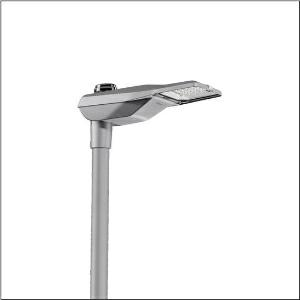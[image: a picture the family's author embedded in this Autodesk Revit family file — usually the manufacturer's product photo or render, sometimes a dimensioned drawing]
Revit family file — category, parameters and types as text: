
# Revit family: streetlight_sl_21_micro___st0_8a_5xe5c37n08db_0c9a
name_source: partatom
category: Lighting Fixtures
units: mm (PartAtom-declared; Revit-internal decimal feet)

## family parameters
Cut with Voids When Loaded = No
Host = Face
Light Source = No
Part Type = Normal
Room Calculation Point = No
Round Connector Dimension = Use Diameter
Shared = No

## types (1)
- --- (1 x LED, 5110 lm, 39.1 W, 3000K)
    Apparent Load = 39 VA
    CIE Flux Codes = 38 75 97 100 100
    Color Rendering = 70
    Color Temperature = 3000K
    Default Elevation = 1800 mm
    Description = Streetlight SL 21 micro, mast luminaire, primary light control with lens, of PMMA, primary optical cover: cover, of toughened safety glass, transparent, light distribution: ST0.8a, light emission: direct distribution, primary light characteristic: asymmetric, installation type: post-top, LED, 3G 1.5mm², High Power LED, rated luminous flux: 5.110lm, luminous efficacy: 131lm/W, light colour: 730, colour temperature: 3000K, control: overheat protection, pre-setting: linear dimming characteristic, constant luminous flux control, time-dependent luminous flux control, flexible luminous flux parameterisation, mains connection: 230..240V, AC, 50/60Hz, connection cable pre-assembled, cable length: 6,5m, wiring characteristics: H07RN-F, start of lifetime: 39W, end of service life: 41W, reduction: 18W, luminaire housing, of diecast aluminium (EN AC-44300), powder-coated, Siteco® metallic grey (DB 702S), corrosivity category C5 mid according to DIN EN ISO 12944, multi-level sealing system, sealing non-destructively replaceable, inclination adjustable: 0°, 5°, 10°, 15°, length: 528mm, width: 235mm, height: 110mm, spigot size: 76/60mm (post-top), protection rating (complete): IP66, insulation class (complete): insulation class I (protective earthing), certification: CE, ENEC, ENEC+, VDE, impact resistance: IK09, permissible operating ambient temperature for outdoor applications: -40..+50°C, standard-compliant lighting for roads and squares, packaging unit: 1 piece

Light Distribution: ST0.8a
    Height = 110 mm
    Lamp = 1 x LED
    Lamp Light Flux = 5110 lm
    Lamp Power = 39.1 W
    Lamp count = 1
    Length = 528 mm
    Luminous efficacy = 131 lm/W
    Manufacturer = Siteco
    ModVariant = No
    Model = 5XE5C37N08DB
    Number of Poles = 1
    OnlyDefault = Yes
    Power Factor = 1
    Product Name = Streetlight SL 21 micro | ST0.8a
    Product group = mast luminaire | pylon top
    ProductGroupID = 6100
    Protection Class = Protection class I
    Protection Degree = IP 66
    RLX_Detail_Level = 1
    RLX_Emergency_Light_Flux = 0 lm
    RLX_Emergency_Type = 0
    RLX_Emergency_Type_DB = No
    RlxData = <blob elided: 98429 chars, md5=3bcf6e8b>
    Socket = socket
    Standby Power = 0 W
    System Light Flux = 5110 lm
    System Power = 39 W
    Type Comments = factory setting: luminous flux: 100 % | dim-lin: 254 | 765 mA
    Type Image = l_1294375.jpg
    URL = http://relux.com
    VarID = @adj_104177
    Voltage = 0 V
    Weight = 0.00 kg
    Width = 235 mm

## geometry (parser evidence)
native form markers: Blend x4, Sweep x12
no freeform markers — native parametric forms only
